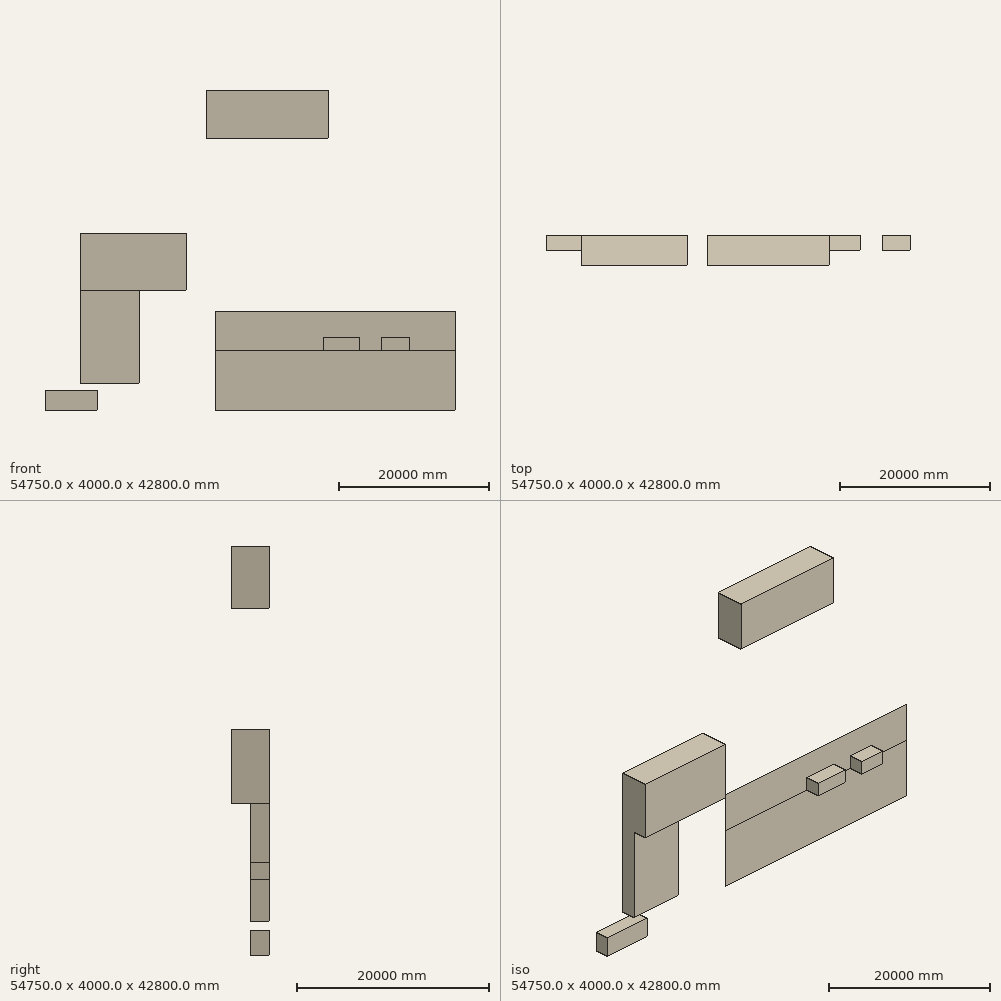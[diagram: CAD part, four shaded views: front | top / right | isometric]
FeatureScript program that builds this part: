
annotation { "Feature Type Name" : "Feature", "Feature Type Description" : "" }
export const myFeature = defineFeature(function(context is Context, id is Id, definition is map)
    precondition{}
    {
        {
            var Q0;
            Q0=qCreatedBy(makeId("Front.planeOp"),FACE);
            var sketch = newSketch(context, id + "F0", { "sketchPlane" : qUnion([Q0])});
            skLineSegment(sketch, "E0.bottom", {"start": v(0, 0) * mm, "end": v(68050, 0) * mm});
            skLineSegment(sketch, "E0.top", {"start": v(0, 44200) * mm, "end": v(68050, 44200) * mm});
            skLineSegment(sketch, "E0.left", {"start": v(0, 0) * mm, "end": v(0, 44200) * mm});
            skLineSegment(sketch, "E0.right", {"start": v(68050, 0) * mm, "end": v(68050, 44200) * mm});
            skLineSegment(sketch, "E1.bottom", {"start": v(34850, 42800) * mm, "end": v(51150, 42800) * mm});
            skLineSegment(sketch, "E1.top", {"start": v(34850, 36300) * mm, "end": v(51150, 36300) * mm});
            skLineSegment(sketch, "E1.left", {"start": v(34850, 42800) * mm, "end": v(34850, 36300) * mm});
            skLineSegment(sketch, "E1.right", {"start": v(51150, 42800) * mm, "end": v(51150, 36300) * mm});
            skLineSegment(sketch, "E2.bottom", {"start": v(18000, 23700) * mm, "end": v(32126.27, 23700) * mm});
            skLineSegment(sketch, "E2.top", {"start": v(25860.59, 16013.65) * mm, "end": v(32126.27, 16013.65) * mm});
            skLineSegment(sketch, "E2.left", {"start": v(18000, 23700) * mm, "end": v(18000, 16013.65) * mm});
            skLineSegment(sketch, "E2.right", {"start": v(32126.27, 23700) * mm, "end": v(32126.27, 16013.65) * mm});
            skLineSegment(sketch, "E3.top", {"start": v(18000, 3700) * mm, "end": v(25860.59, 3700) * mm});
            skLineSegment(sketch, "E3.left", {"start": v(18000, 16013.65) * mm, "end": v(18000, 3700) * mm});
            skLineSegment(sketch, "E3.right", {"start": v(25860.59, 16013.65) * mm, "end": v(25860.59, 3700) * mm});
            skLineSegment(sketch, "E4.bottom", {"start": v(13300, 2700) * mm, "end": v(20303.81, 2700) * mm});
            skLineSegment(sketch, "E4.top", {"start": v(13300, 55.8) * mm, "end": v(20303.81, 55.8) * mm});
            skLineSegment(sketch, "E4.left", {"start": v(13300, 2700) * mm, "end": v(13300, 55.8) * mm});
            skLineSegment(sketch, "E4.right", {"start": v(20303.81, 2700) * mm, "end": v(20303.81, 55.8) * mm});
            skLineSegment(sketch, "E5.top", {"start": v(35650, 0) * mm, "end": v(68050, 0) * mm});
            skLineSegment(sketch, "E6.bottom", {"start": v(68050, 8000) * mm, "end": v(36055.75, 8000) * mm});
            skLineSegment(sketch, "E6.top", {"start": v(68050, -48.7) * mm, "end": v(36055.75, -48.7) * mm});
            skLineSegment(sketch, "E6.left", {"start": v(68050, 8000) * mm, "end": v(68050, -48.7) * mm});
            skLineSegment(sketch, "E6.right", {"start": v(36055.75, 8000) * mm, "end": v(36055.75, -48.7) * mm});
            skLineSegment(sketch, "E7.bottom", {"start": v(61850, 8000) * mm, "end": v(58150, 8000) * mm});
            skLineSegment(sketch, "E7.top", {"start": v(61850, 9800) * mm, "end": v(58150, 9800) * mm});
            skLineSegment(sketch, "E7.left", {"start": v(61850, 8000) * mm, "end": v(61850, 9800) * mm});
            skLineSegment(sketch, "E7.right", {"start": v(58150, 8000) * mm, "end": v(58150, 9800) * mm});
            skLineSegment(sketch, "E8.bottom", {"start": v(55250, 8000) * mm, "end": v(50450, 8000) * mm});
            skLineSegment(sketch, "E8.top", {"start": v(55250, 9800) * mm, "end": v(50450, 9800) * mm});
            skLineSegment(sketch, "E8.left", {"start": v(55250, 8000) * mm, "end": v(55250, 9800) * mm});
            skLineSegment(sketch, "E8.right", {"start": v(50450, 8000) * mm, "end": v(50450, 9800) * mm});
            skLineSegment(sketch, "E9.bottom", {"start": v(36055.75, 8000) * mm, "end": v(68050, 8000) * mm});
            skLineSegment(sketch, "E9.top", {"start": v(36055.75, 13200) * mm, "end": v(68050, 13200) * mm});
            skLineSegment(sketch, "E9.left", {"start": v(36055.75, 8000) * mm, "end": v(36055.75, 13200) * mm});
            skLineSegment(sketch, "E9.right", {"start": v(68050, 8000) * mm, "end": v(68050, 13200) * mm});
            skLineSegment(sketch, "E10", {"start": v(18000, 16013.65) * mm, "end": v(25860.59, 16013.65) * mm});
            skSolve(sketch);
        }
        {
            var Q0;
            Q0=makeQuery(id+"F0.imprint","IMPRINT",FACE,{"disambiguationData":[TD([[makeQuery(id+"F0.imprint","IMPRINT",EDGE,{"derivedFrom":sQuery(id+"F0.wireOp",EDGE,"E2.bottom")}),-1.0]])]});
            var Q1;
            Q1=makeQuery(id+"F0.imprint","IMPRINT",FACE,{"disambiguationData":[TD([[makeQuery(id+"F0.imprint","IMPRINT",EDGE,{"derivedFrom":sQuery(id+"F0.wireOp",EDGE,"E1.bottom")}),-1.0]])]});
            extrude(context, id + "F1", {"entities" : qUnion([Q0, Q1]), "depth" : 4000 * mm, "offsetDistance" : 25 * mm});
        }
        {
            var Q0;
            Q0=makeQuery(id+"F0.imprint","IMPRINT",FACE,{"disambiguationData":[TD([[makeQuery(id+"F0.imprint","IMPRINT",EDGE,{"derivedFrom":sQuery(id+"F0.wireOp",EDGE,"E7.top")}),-1.0]])]});
            extrude(context, id + "F2", {"entities" : qUnion([Q0]), "operationType" : NewBodyOperationType.ADD, "depth" : 15 * mm, "offsetDistance" : 25 * mm});
        }
        {
            var Q0;
            {var subQ1=sQuery(id+"F0.wireOp",EDGE,"E0.bottom");Q0=makeQuery(id+"F0.imprint","IMPRINT",FACE,{"disambiguationData":[TD([[makeQuery(id+"F0.imprint","IMPRINT",EDGE,{"derivedFrom":subQ1}),1.0]])]});}
            extrude(context, id + "F3", {"entities" : qUnion([Q0]), "depth" : 5 * mm, "offsetDistance" : 25 * mm});
        }
        {
            var Q0;
            Q0=makeQuery(id+"F0.imprint","IMPRINT",FACE,{"disambiguationData":[TD([[makeQuery(id+"F0.imprint","IMPRINT",EDGE,{"derivedFrom":sQuery(id+"F0.wireOp",EDGE,"E7.top")}),-1.0]])]});
            extrude(context, id + "F4", {"entities" : qUnion([Q0]), "operationType" : NewBodyOperationType.ADD, "depth" : 15 * mm, "offsetDistance" : 25 * mm});
        }
        {
            var Q0;
            {var subQ3=sQuery(id+"F0.wireOp",EDGE,"E5.top");var subQ8=sQuery(id+"F0.wireOp",EDGE,"E6.left");var subQ9=makeQuery(id+"F0.imprint","INTERSECT",VERTEX,{"derivedFrom":[subQ3,subQ8]});Q0=makeQuery(id+"F0.imprint","IMPRINT",FACE,{"disambiguationData":[TD([[makeQuery(id+"F0.imprint","IMPRINT",EDGE,{"disambiguationData":[TD([[subQ9,1.0]])],"derivedFrom":subQ3}),1.0]])]});}
            var Q1;
            Q1=makeQuery(id+"F0.imprint","IMPRINT",FACE,{"disambiguationData":[TD([[makeQuery(id+"F0.imprint","IMPRINT",EDGE,{"derivedFrom":sQuery(id+"F0.wireOp",EDGE,"E8.top")}),1.0]])]});
            var Q2;
            Q2=makeQuery(id+"F0.imprint","IMPRINT",FACE,{"disambiguationData":[TD([[makeQuery(id+"F0.imprint","IMPRINT",EDGE,{"derivedFrom":sQuery(id+"F0.wireOp",EDGE,"E7.top")}),1.0]])]});
            var Q3;
            Q3=makeQuery(id+"F0.imprint","IMPRINT",FACE,{"disambiguationData":[TD([[makeQuery(id+"F0.imprint","IMPRINT",EDGE,{"derivedFrom":sQuery(id+"F0.wireOp",EDGE,"E3.top")}),1.0]])]});
            var Q4;
            Q4=makeQuery(id+"F0.imprint","IMPRINT",FACE,{"disambiguationData":[TD([[makeQuery(id+"F0.imprint","IMPRINT",EDGE,{"derivedFrom":sQuery(id+"F0.wireOp",EDGE,"E4.bottom")}),-1.0]])]});
            extrude(context, id + "F5", {"entities" : qUnion([Q0, Q1, Q2, Q3, Q4]), "operationType" : NewBodyOperationType.ADD, "depth" : 2000 * mm, "offsetDistance" : 25 * mm});
        }
    });
